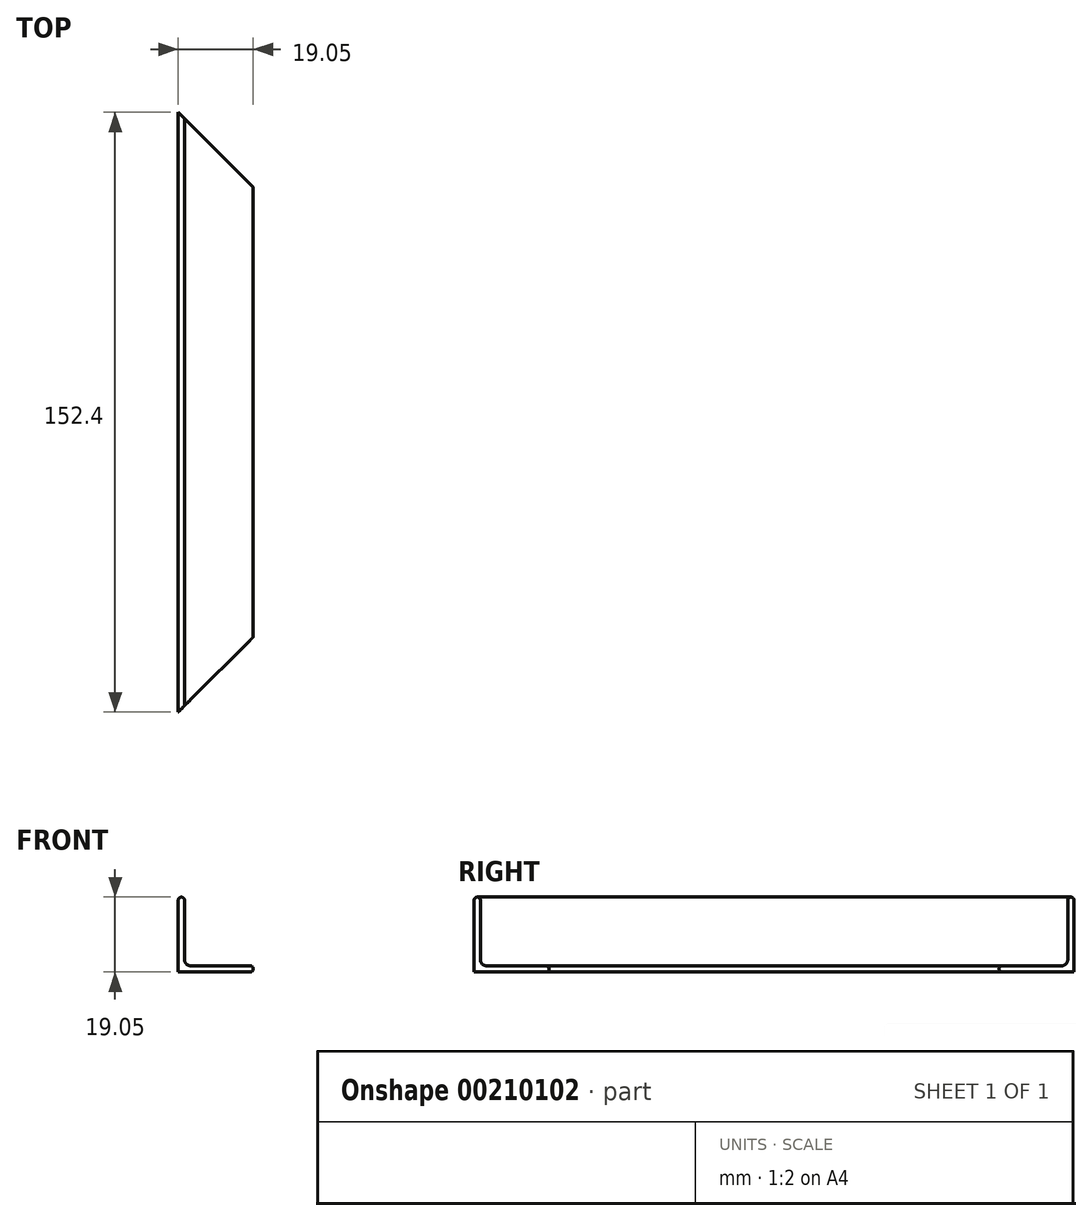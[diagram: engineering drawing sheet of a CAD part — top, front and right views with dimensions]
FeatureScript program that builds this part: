
annotation { "Feature Type Name" : "Feature", "Feature Type Description" : "" }
export const myFeature = defineFeature(function(context is Context, id is Id, definition is map)
    precondition{}
    {
        {
            var Q0;
            Q0=qCreatedBy(makeId("Front.planeOp"),FACE);
            var sketch = newSketch(context, id + "F0", { "sketchPlane" : qUnion([Q0])});
            skLineSegment(sketch, "E0", {"start": v(0, 0) * mm, "end": v(18.26, 0) * mm});
            skLineSegment(sketch, "E1", {"start": v(0, 0) * mm, "end": v(0, 18.26) * mm});
            skLineSegment(sketch, "E2.0", {"start": v(1.59, 3.18) * mm, "end": v(1.59, 18.26) * mm});
            skLineSegment(sketch, "E3.0", {"start": v(3.18, 1.59) * mm, "end": v(18.26, 1.59) * mm});
            skLineSegment(sketch, "E4", {"start": v(0.8, 19.05) * mm, "end": v(0.8, 19.05) * mm});
            skLineSegment(sketch, "E5", {"start": v(19.05, 0.8) * mm, "end": v(19.05, 0.8) * mm});
            skPoint(sketch, "E6.visualSharp", {"position": v(1.59, 19.05) * mm});
            skArc(sketch, "E6.filletArc", {"start": v(1.59, 18.26) * mm, "mid": v(1.36, 18.82) * mm, "end": v(0.8, 19.05) * mm});
            skPoint(sketch, "E7.visualSharp", {"position": v(0, 19.05) * mm});
            skArc(sketch, "E7.filletArc", {"start": v(0.8, 19.05) * mm, "mid": v(0.23, 18.82) * mm, "end": v(0, 18.26) * mm});
            skPoint(sketch, "E8.visualSharp", {"position": v(19.05, 1.59) * mm});
            skArc(sketch, "E8.filletArc", {"start": v(19.05, 0.8) * mm, "mid": v(18.82, 1.36) * mm, "end": v(18.26, 1.59) * mm});
            skPoint(sketch, "E9.visualSharp", {"position": v(19.05, 0) * mm});
            skArc(sketch, "E9.filletArc", {"start": v(18.26, 0) * mm, "mid": v(18.82, 0.23) * mm, "end": v(19.05, 0.8) * mm});
            skPoint(sketch, "E10.visualSharp", {"position": v(1.59, 1.59) * mm});
            skArc(sketch, "E10.filletArc", {"start": v(1.59, 3.18) * mm, "mid": v(2.05, 2.05) * mm, "end": v(3.18, 1.59) * mm});
            skSolve(sketch);
        }
        {
            var Q0;
            Q0 = qSketchRegion(id + "F0", true);
            extrude(context, id + "F1", {"entities" : qUnion([Q0]), "depth" : 152.4 * mm});
        }
        {
            var Q0;
            Q0=qCreatedBy(makeId("Top.planeOp"),FACE);
            var sketch = newSketch(context, id + "F2", { "sketchPlane" : qUnion([Q0])});
            skLineSegment(sketch, "E11", {"start": v(0, 0) * mm, "end": v(29.7, -29.7) * mm});
            skLineSegment(sketch, "E12", {"start": v(29.7, -29.7) * mm, "end": v(30.35, 0) * mm});
            skLineSegment(sketch, "E13", {"start": v(30.35, 0) * mm, "end": v(0, 0) * mm});
            skLineSegment(sketch, "E14", {"start": v(0, -152.4) * mm, "end": v(26.34, -126.06) * mm});
            skLineSegment(sketch, "E15", {"start": v(0, -152.4) * mm, "end": v(26.34, -152.4) * mm});
            skLineSegment(sketch, "E16", {"start": v(26.34, -126.06) * mm, "end": v(26.34, -152.4) * mm});
            skSolve(sketch);
        }
        {
            var Q0;
            Q0 = qSketchRegion(id + "F2", true);
            extrude(context, id + "F3", {"entities" : qUnion([Q0]), "operationType" : NewBodyOperationType.REMOVE, "endBound" : BoundingType.THROUGH_ALL, "depth" : 25.4 * mm});
        }
    });
